# Revit family: Sanitary_Showers_hansgrohe_26278XXX-Vernis-Blend-Shower-holder-set_01
name_source: partatom
category: Plumbing Fixtures
units: mm (PartAtom-declared; Revit-internal decimal feet)

## family parameters
Always vertical = No
Cut with Voids When Loaded = No
OmniClass Number = 23.31.17.00
OmniClass Title = Showers
Part Type = Normal
Room Calculation Point = No
Round Connector Dimension = Use Diameter
Shared = No
Work Plane-Based = Yes

## types (1)
- 000 Chrome
    Default Elevation = 1219 mm
    Description = Vernis Blend Shower holder set 100 Vario EcoSmart with shower hose 160 cm
    Manufacturer = Hansgrohe
    Material = Hansgrohe - Metal - 000 Chrome
    Material 1 = Hansgrohe - Plastic - Gray
    Model = 26278XXX
    Product Guid = c07d29fd-eaa2-42ca-b3d5-bc6e3b8bfba5
    Product Page URL = https://pro.hansgrohe.com
    Product data url = https://bimobject.com
    URL = https://www.hansgrohe.com
    Version = 1

## geometry (parser evidence)
native form markers: Blend x6, Sweep x1
no freeform markers — native parametric forms only
